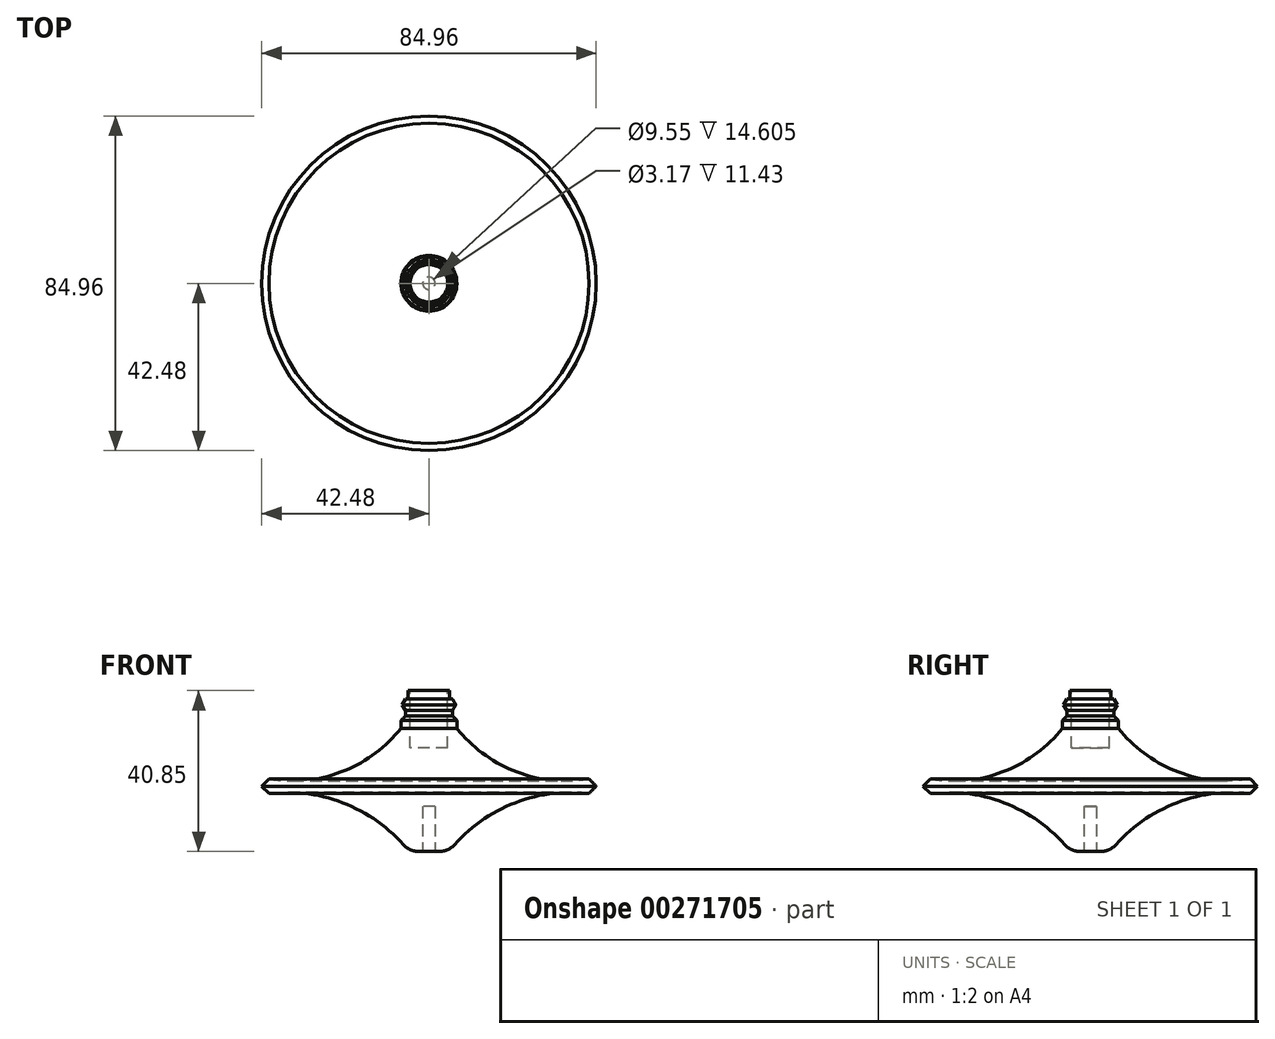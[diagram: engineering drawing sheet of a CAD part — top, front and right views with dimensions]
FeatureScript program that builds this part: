
annotation { "Feature Type Name" : "Feature", "Feature Type Description" : "" }
export const myFeature = defineFeature(function(context is Context, id is Id, definition is map)
    precondition{}
    {
        {
            var Q0;
            Q0=qCreatedBy(makeId("Right.planeOp"),FACE);
            var sketch = newSketch(context, id + "F0", { "sketchPlane" : qUnion([Q0])});
            skLineSegment(sketch, "E0", {"start": v(0, 0) * mm, "end": v(5.07, 0) * mm});
            skArc(sketch, "E1", {"start": v(40.68, 14.77) * mm, "mid": v(20.97, 11.99) * mm, "end": v(5.07, 0) * mm});
            skLineSegment(sketch, "E2", {"start": v(40.68, 14.77) * mm, "end": v(42.48, 16.57) * mm});
            skLineSegment(sketch, "E3", {"start": v(42.48, 16.57) * mm, "end": v(40.68, 18.38) * mm});
            skArc(sketch, "E4", {"start": v(7.1, 31.27) * mm, "mid": v(22.13, 20.24) * mm, "end": v(40.68, 18.38) * mm});
            skLineSegment(sketch, "E5", {"start": v(7.1, 31.27) * mm, "end": v(7.1, 34.52) * mm});
            skLineSegment(sketch, "E6", {"start": v(7.1, 34.52) * mm, "end": v(5.97, 34.52) * mm});
            skLineSegment(sketch, "E7", {"start": v(5.97, 34.52) * mm, "end": v(5.97, 35.81) * mm});
            skLineSegment(sketch, "E8", {"start": v(5.97, 35.81) * mm, "end": v(6.83, 37.25) * mm});
            skLineSegment(sketch, "E9", {"start": v(6.83, 37.25) * mm, "end": v(5.97, 38.74) * mm});
            skLineSegment(sketch, "E10", {"start": v(5.97, 38.74) * mm, "end": v(5.25, 38.74) * mm});
            skLineSegment(sketch, "E11", {"start": v(5.25, 38.74) * mm, "end": v(5.25, 40.85) * mm});
            skLineSegment(sketch, "E12", {"start": v(5.25, 40.85) * mm, "end": v(0, 40.85) * mm});
            skLineSegment(sketch, "E13", {"start": v(0, 40.85) * mm, "end": v(0, 0) * mm});
            skSolve(sketch);
        }
        {
            var Q0;
            Q0=makeQuery(id+"F0.imprint","IMPRINT",FACE,{"disambiguationData":[TD([[makeQuery(id+"F0.imprint","IMPRINT",EDGE,{"derivedFrom":sQuery(id+"F0.wireOp",EDGE,"E0")}),1.0]])]});
            var Q1;
            Q1=sQuery(id+"F0.wireOp",EDGE,"E13");
            revolve(context, id + "F1", {"entities" : qUnion([Q0]), "axis" : qUnion([Q1]), "revolveType" : RevolveType.FULL});
        }
        {
            var Q0;
            Q0=makeQuery(id+"F1.opRevolve","SWEPT_EDGE",EDGE,{"disambiguationData":[OSD([sQuery(id+"F0.wireOp",EDGE,"E0"),sQuery(id+"F0.wireOp",EDGE,"E1")])]});
            fillet(context, id + "F2", {"entities" : qUnion([Q0]), "radius" : 5.08 * mm, "tangentPropagation" : true, "allowEdgeOverflow" : false});
        }
        {
            var Q0;
            Q0=makeQuery(id+"F1.opRevolve","SWEPT_EDGE",EDGE,{"disambiguationData":[OSD([sQuery(id+"F0.wireOp",EDGE,"E5"),sQuery(id+"F0.wireOp",EDGE,"E6")])]});
            chamfer(context, id + "F3", {"entities" : qUnion([Q0]), "width" : 1.27 * mm, "tangentPropagation" : true});
        }
        {
            var Q0;
            Q0=makeQuery(id+"F1.opRevolve","SWEPT_FACE",FACE,{"disambiguationData":[OSD([sQuery(id+"F0.wireOp",EDGE,"E12")])]});
            var sketch = newSketch(context, id + "F4", { "sketchPlane" : qUnion([Q0])});
            skCircle(sketch, "E14", {"center": v(0, 0) * mm, "radius": 4.78 * mm});
            skSolve(sketch);
        }
        {
            var Q0;
            Q0=makeQuery(id+"F4.imprint","IMPRINT",FACE,{"disambiguationData":[TD([[makeQuery(id+"F4.imprint","IMPRINT",EDGE,{"derivedFrom":sQuery(id+"F4.wireOp",EDGE,"E14")}),1.0]])]});
            extrude(context, id + "F5", {"entities" : qUnion([Q0]), "operationType" : NewBodyOperationType.REMOVE, "oppositeDirection" : true, "depth" : 14.6 * mm});
        }
        {
            var Q0;
            Q0=makeQuery(id+"F1.opRevolve","SWEPT_FACE",FACE,{"disambiguationData":[OSD([sQuery(id+"F0.wireOp",EDGE,"E0")])]});
            var sketch = newSketch(context, id + "F6", { "sketchPlane" : qUnion([Q0])});
            skCircle(sketch, "E15", {"center": v(0, 0) * mm, "radius": 1.6 * mm});
            skSolve(sketch);
        }
        {
            var Q0;
            Q0=makeQuery(id+"F6.imprint","IMPRINT",FACE,{"disambiguationData":[TD([[makeQuery(id+"F6.imprint","IMPRINT",EDGE,{"derivedFrom":sQuery(id+"F6.wireOp",EDGE,"E15")}),1.0]])]});
            extrude(context, id + "F7", {"entities" : qUnion([Q0]), "operationType" : NewBodyOperationType.ADD, "oppositeDirection" : true, "depth" : 11.43 * mm});
        }
        {
            var Q0;
            Q0=qCreatedBy(makeId("Top.planeOp"),FACE);
            var sketch = newSketch(context, id + "F8", { "sketchPlane" : qUnion([Q0])});
            skCircle(sketch, "E16", {"center": v(0, 0) * mm, "radius": 1.59 * mm});
            skSolve(sketch);
        }
        {
            var Q0;
            Q0=makeQuery(id+"F8.imprint","IMPRINT",FACE,{"disambiguationData":[TD([[makeQuery(id+"F8.imprint","IMPRINT",EDGE,{"derivedFrom":sQuery(id+"F8.wireOp",EDGE,"E16")}),1.0]])]});
            extrude(context, id + "F9", {"entities" : qUnion([Q0]), "operationType" : NewBodyOperationType.REMOVE, "depth" : 11.43 * mm});
        }
    });
